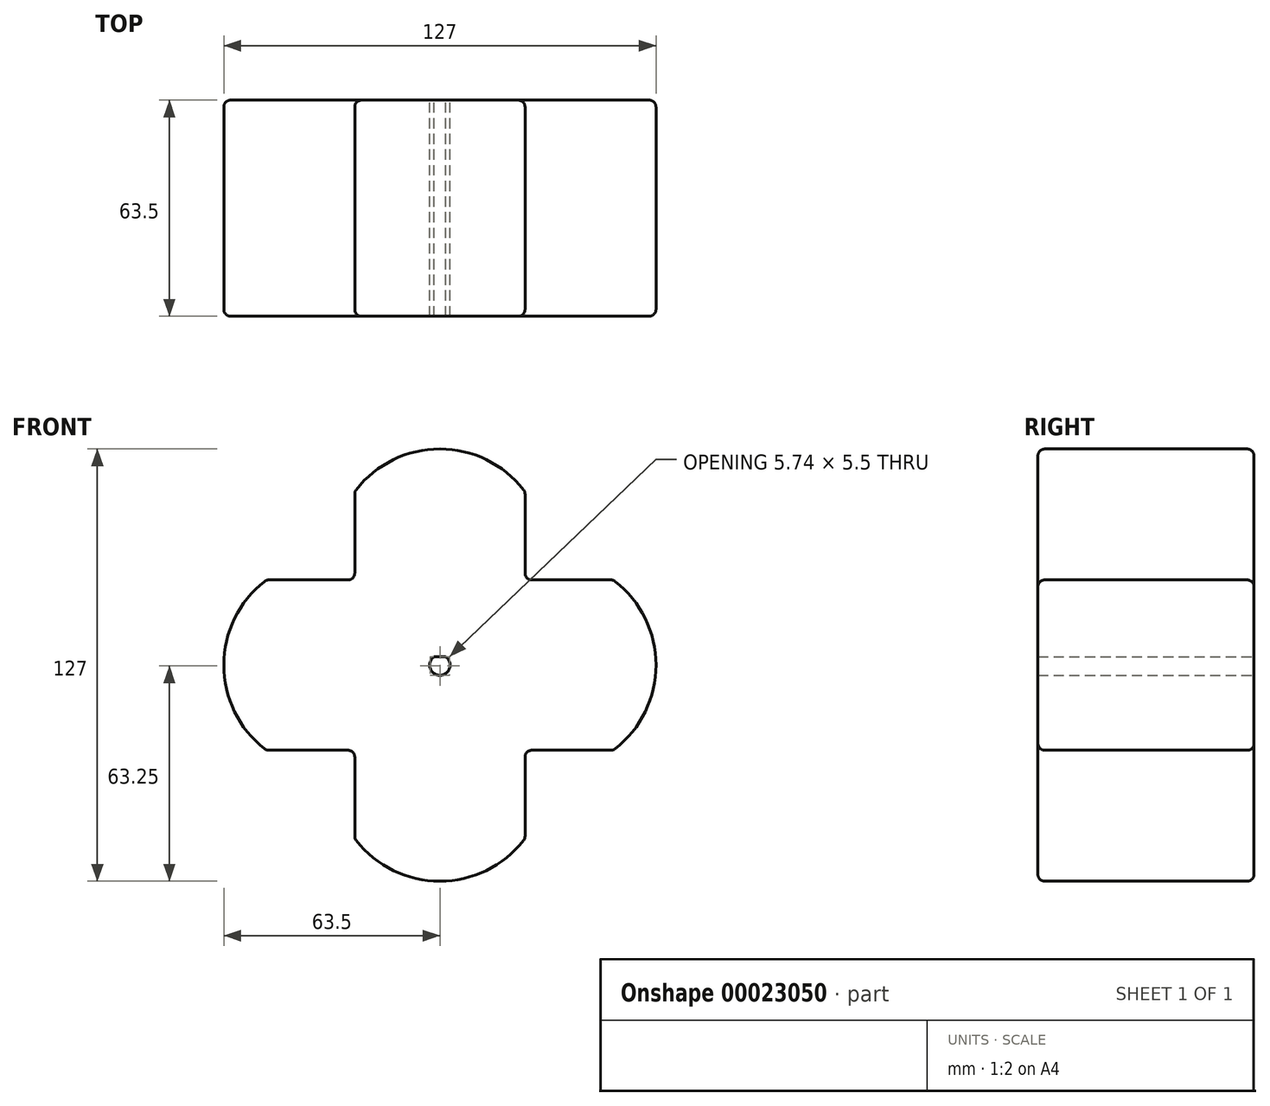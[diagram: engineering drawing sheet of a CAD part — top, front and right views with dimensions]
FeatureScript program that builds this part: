
annotation { "Feature Type Name" : "Feature", "Feature Type Description" : "" }
export const myFeature = defineFeature(function(context is Context, id is Id, definition is map)
    precondition{}
    {
        {
            var Q0;
            Q0=qCreatedBy(makeId("Front.planeOp"),FACE);
            var sketch = newSketch(context, id + "F0", { "sketchPlane" : qUnion([Q0])});
            skLineSegment(sketch, "E0", {"start": v(0, 63.5) * mm, "end": v(0, 0) * mm});
            skLineSegment(sketch, "E1", {"start": v(0, 0) * mm, "end": v(0, -63.5) * mm});
            skPoint(sketch, "E2", {"position": v(-38.48, 0) * mm});
            skPoint(sketch, "E3", {"position": v(0, 38.48) * mm});
            skPoint(sketch, "E4", {"position": v(38.48, 0) * mm});
            skPoint(sketch, "E5", {"position": v(0, -38.48) * mm});
            skLineSegment(sketch, "E6", {"start": v(-38.48, 25.02) * mm, "end": v(-25.02, 25.02) * mm});
            skLineSegment(sketch, "E7", {"start": v(-38.48, -25.02) * mm, "end": v(-25.02, -25.02) * mm});
            skLineSegment(sketch, "E8", {"start": v(-25.02, 38.48) * mm, "end": v(-25.02, 25.02) * mm});
            skLineSegment(sketch, "E9", {"start": v(25.02, 38.48) * mm, "end": v(25.02, 25.02) * mm});
            skLineSegment(sketch, "E10.trimOffspring", {"start": v(25.02, 25.02) * mm, "end": v(38.48, 25.02) * mm});
            skLineSegment(sketch, "E11.trimOffspring", {"start": v(25.02, 0) * mm, "end": v(63.5, 0) * mm});
            skLineSegment(sketch, "E12.trimOffspring", {"start": v(-25.02, 0) * mm, "end": v(-63.5, 0) * mm});
            skLineSegment(sketch, "E13.trimOffspring", {"start": v(25.02, -25.02) * mm, "end": v(38.48, -25.02) * mm});
            skLineSegment(sketch, "E14.trimOffspring", {"start": v(-25.02, -25.02) * mm, "end": v(-25.02, -38.48) * mm});
            skLineSegment(sketch, "E15.trimOffspring", {"start": v(25.02, -25.02) * mm, "end": v(25.02, -38.48) * mm});
            skPoint(sketch, "E16", {"position": v(0, -51) * mm});
            skPoint(sketch, "E17", {"position": v(-51, 0) * mm});
            skPoint(sketch, "E18", {"position": v(51, 0) * mm});
            skPoint(sketch, "E19", {"position": v(0, 51) * mm});
            skLineSegment(sketch, "E20", {"start": v(-38.48, 25.02) * mm, "end": v(-51, 25.02) * mm});
            skLineSegment(sketch, "E21", {"start": v(-38.48, -25.02) * mm, "end": v(-51, -25.02) * mm});
            skLineSegment(sketch, "E22", {"start": v(-25.02, -38.48) * mm, "end": v(-25.02, -51) * mm});
            skLineSegment(sketch, "E23", {"start": v(25.02, -38.48) * mm, "end": v(25.02, -51) * mm});
            skLineSegment(sketch, "E24", {"start": v(38.48, -25.02) * mm, "end": v(51, -25.02) * mm});
            skLineSegment(sketch, "E25", {"start": v(38.48, 25.02) * mm, "end": v(51, 25.02) * mm});
            skLineSegment(sketch, "E26", {"start": v(25.02, 38.48) * mm, "end": v(25.02, 51) * mm});
            skLineSegment(sketch, "E27", {"start": v(-25.02, 38.48) * mm, "end": v(-25.02, 51) * mm});
            skArc(sketch, "E28", {"start": v(-51, 25.02) * mm, "mid": v(-63.5, 0) * mm, "end": v(-51, -25.02) * mm});
            skArc(sketch, "E29", {"start": v(25.02, 51) * mm, "mid": v(0, 63.5) * mm, "end": v(-25.02, 51) * mm});
            skArc(sketch, "E30", {"start": v(51, -25.02) * mm, "mid": v(63.5, 0) * mm, "end": v(51, 25.02) * mm});
            skArc(sketch, "E31", {"start": v(-25.02, -51) * mm, "mid": v(0, -63.5) * mm, "end": v(25.02, -51) * mm});
            skArc(sketch, "E32", {"start": v(-1.66, 2.5) * mm, "mid": v(0, -3) * mm, "end": v(1.66, 2.5) * mm});
            skLineSegment(sketch, "E33", {"start": v(0, 2.5) * mm, "end": v(1.66, 2.5) * mm});
            skLineSegment(sketch, "E34", {"start": v(1.66, 2.5) * mm, "end": v(-1.66, 2.5) * mm});
            skSolve(sketch);
        }
        {
            var Q0;
            Q0 = qSketchRegion(id + "F0", true);
            extrude(context, id + "F1", {"entities" : qUnion([Q0]), "depth" : 63.5 * mm});
        }
        {
            var Q0;
            Q0=makeQuery(id+"F1.opExtrude","CAP_EDGE",EDGE,{"disambiguationData":[OSD([sQuery(id+"F0.wireOp",EDGE,"E8"),sQuery(id+"F0.wireOp",EDGE,"E27")])],"isStart":false});
            var Q1;
            Q1=makeQuery(id+"F1.opExtrude","CAP_EDGE",EDGE,{"disambiguationData":[OSD([sQuery(id+"F0.wireOp",EDGE,"E6"),sQuery(id+"F0.wireOp",EDGE,"E20")])],"isStart":false});
            var Q2;
            Q2=makeQuery(id+"F1.opExtrude","CAP_EDGE",EDGE,{"disambiguationData":[OSD([sQuery(id+"F0.wireOp",EDGE,"E29")])],"isStart":false});
            var Q3;
            Q3=makeQuery(id+"F1.opExtrude","CAP_EDGE",EDGE,{"disambiguationData":[OSD([sQuery(id+"F0.wireOp",EDGE,"E10.trimOffspring"),sQuery(id+"F0.wireOp",EDGE,"E25")])],"isStart":false});
            var Q4;
            Q4=makeQuery(id+"F1.opExtrude","CAP_EDGE",EDGE,{"disambiguationData":[OSD([sQuery(id+"F0.wireOp",EDGE,"E9"),sQuery(id+"F0.wireOp",EDGE,"E26")])],"isStart":false});
            var Q5;
            Q5=makeQuery(id+"F1.opExtrude","CAP_EDGE",EDGE,{"disambiguationData":[OSD([sQuery(id+"F0.wireOp",EDGE,"E29")])],"isStart":true});
            var Q6;
            Q6=makeQuery(id+"F1.opExtrude","CAP_EDGE",EDGE,{"disambiguationData":[OSD([sQuery(id+"F0.wireOp",EDGE,"E9"),sQuery(id+"F0.wireOp",EDGE,"E26")])],"isStart":true});
            var Q7;
            Q7=makeQuery(id+"F1.opExtrude","CAP_EDGE",EDGE,{"disambiguationData":[OSD([sQuery(id+"F0.wireOp",EDGE,"E6"),sQuery(id+"F0.wireOp",EDGE,"E20")])],"isStart":true});
            var Q8;
            Q8=makeQuery(id+"F1.opExtrude","CAP_EDGE",EDGE,{"disambiguationData":[OSD([sQuery(id+"F0.wireOp",EDGE,"E8"),sQuery(id+"F0.wireOp",EDGE,"E27")])],"isStart":true});
            var Q9;
            Q9=makeQuery(id+"F1.opExtrude","CAP_EDGE",EDGE,{"disambiguationData":[OSD([sQuery(id+"F0.wireOp",EDGE,"E10.trimOffspring"),sQuery(id+"F0.wireOp",EDGE,"E25")])],"isStart":true});
            var Q10;
            Q10=makeQuery(id+"F1.opExtrude","CAP_EDGE",EDGE,{"disambiguationData":[OSD([sQuery(id+"F0.wireOp",EDGE,"E15.trimOffspring"),sQuery(id+"F0.wireOp",EDGE,"E23")])],"isStart":false});
            var Q11;
            Q11=makeQuery(id+"F1.opExtrude","CAP_EDGE",EDGE,{"disambiguationData":[OSD([sQuery(id+"F0.wireOp",EDGE,"E14.trimOffspring"),sQuery(id+"F0.wireOp",EDGE,"E22")])],"isStart":false});
            var Q12;
            Q12=makeQuery(id+"F1.opExtrude","CAP_EDGE",EDGE,{"disambiguationData":[OSD([sQuery(id+"F0.wireOp",EDGE,"E13.trimOffspring"),sQuery(id+"F0.wireOp",EDGE,"E24")])],"isStart":false});
            var Q13;
            Q13=makeQuery(id+"F1.opExtrude","CAP_EDGE",EDGE,{"disambiguationData":[OSD([sQuery(id+"F0.wireOp",EDGE,"E7"),sQuery(id+"F0.wireOp",EDGE,"E21")])],"isStart":false});
            var Q14;
            Q14=makeQuery(id+"F1.opExtrude","CAP_EDGE",EDGE,{"disambiguationData":[OSD([sQuery(id+"F0.wireOp",EDGE,"E31")])],"isStart":false});
            var Q15;
            Q15=makeQuery(id+"F1.opExtrude","CAP_EDGE",EDGE,{"disambiguationData":[OSD([sQuery(id+"F0.wireOp",EDGE,"E31")])],"isStart":true});
            var Q16;
            Q16=makeQuery(id+"F1.opExtrude","CAP_EDGE",EDGE,{"disambiguationData":[OSD([sQuery(id+"F0.wireOp",EDGE,"E7"),sQuery(id+"F0.wireOp",EDGE,"E21")])],"isStart":true});
            var Q17;
            Q17=makeQuery(id+"F1.opExtrude","CAP_EDGE",EDGE,{"disambiguationData":[OSD([sQuery(id+"F0.wireOp",EDGE,"E15.trimOffspring"),sQuery(id+"F0.wireOp",EDGE,"E23")])],"isStart":true});
            var Q18;
            Q18=makeQuery(id+"F1.opExtrude","CAP_EDGE",EDGE,{"disambiguationData":[OSD([sQuery(id+"F0.wireOp",EDGE,"E14.trimOffspring"),sQuery(id+"F0.wireOp",EDGE,"E22")])],"isStart":true});
            var Q19;
            Q19=makeQuery(id+"F1.opExtrude","CAP_EDGE",EDGE,{"disambiguationData":[OSD([sQuery(id+"F0.wireOp",EDGE,"E13.trimOffspring"),sQuery(id+"F0.wireOp",EDGE,"E24")])],"isStart":true});
            var Q20;
            Q20=makeQuery(id+"F1.opExtrude","CAP_EDGE",EDGE,{"disambiguationData":[OSD([sQuery(id+"F0.wireOp",EDGE,"E30")])],"isStart":false});
            var Q21;
            Q21=makeQuery(id+"F1.opExtrude","CAP_EDGE",EDGE,{"disambiguationData":[OSD([sQuery(id+"F0.wireOp",EDGE,"E30")])],"isStart":true});
            var Q22;
            Q22=makeQuery(id+"F1.opExtrude","CAP_EDGE",EDGE,{"disambiguationData":[OSD([sQuery(id+"F0.wireOp",EDGE,"E28")])],"isStart":false});
            var Q23;
            Q23=makeQuery(id+"F1.opExtrude","CAP_EDGE",EDGE,{"disambiguationData":[OSD([sQuery(id+"F0.wireOp",EDGE,"E28")])],"isStart":true});
            var Q24;
            Q24=makeQuery(id+"F1.opExtrude","SWEPT_EDGE",EDGE,{"disambiguationData":[OSD([sQuery(id+"F0.wireOp",EDGE,"E20"),sQuery(id+"F0.wireOp",EDGE,"E28")])]});
            var Q25;
            Q25=makeQuery(id+"F1.opExtrude","SWEPT_EDGE",EDGE,{"disambiguationData":[OSD([sQuery(id+"F0.wireOp",EDGE,"E27"),sQuery(id+"F0.wireOp",EDGE,"E29")])]});
            var Q26;
            Q26=makeQuery(id+"F1.opExtrude","SWEPT_EDGE",EDGE,{"disambiguationData":[OSD([sQuery(id+"F0.wireOp",EDGE,"E26"),sQuery(id+"F0.wireOp",EDGE,"E29")])]});
            var Q27;
            Q27=makeQuery(id+"F1.opExtrude","SWEPT_EDGE",EDGE,{"disambiguationData":[OSD([sQuery(id+"F0.wireOp",EDGE,"E6"),sQuery(id+"F0.wireOp",EDGE,"E8")])]});
            var Q28;
            Q28=makeQuery(id+"F1.opExtrude","SWEPT_EDGE",EDGE,{"disambiguationData":[OSD([sQuery(id+"F0.wireOp",EDGE,"E9"),sQuery(id+"F0.wireOp",EDGE,"E10.trimOffspring")])]});
            var Q29;
            Q29=makeQuery(id+"F1.opExtrude","SWEPT_EDGE",EDGE,{"disambiguationData":[OSD([sQuery(id+"F0.wireOp",EDGE,"E25"),sQuery(id+"F0.wireOp",EDGE,"E30")])]});
            var Q30;
            Q30=makeQuery(id+"F1.opExtrude","SWEPT_EDGE",EDGE,{"disambiguationData":[OSD([sQuery(id+"F0.wireOp",EDGE,"E22"),sQuery(id+"F0.wireOp",EDGE,"E31")])]});
            var Q31;
            Q31=makeQuery(id+"F1.opExtrude","SWEPT_EDGE",EDGE,{"disambiguationData":[OSD([sQuery(id+"F0.wireOp",EDGE,"E21"),sQuery(id+"F0.wireOp",EDGE,"E28")])]});
            var Q32;
            Q32=makeQuery(id+"F1.opExtrude","SWEPT_EDGE",EDGE,{"disambiguationData":[OSD([sQuery(id+"F0.wireOp",EDGE,"E23"),sQuery(id+"F0.wireOp",EDGE,"E31")])]});
            var Q33;
            Q33=makeQuery(id+"F1.opExtrude","SWEPT_EDGE",EDGE,{"disambiguationData":[OSD([sQuery(id+"F0.wireOp",EDGE,"E7"),sQuery(id+"F0.wireOp",EDGE,"E14.trimOffspring")])]});
            var Q34;
            Q34=makeQuery(id+"F1.opExtrude","SWEPT_EDGE",EDGE,{"disambiguationData":[OSD([sQuery(id+"F0.wireOp",EDGE,"E13.trimOffspring"),sQuery(id+"F0.wireOp",EDGE,"E15.trimOffspring")])]});
            var Q35;
            Q35=makeQuery(id+"F1.opExtrude","SWEPT_EDGE",EDGE,{"disambiguationData":[OSD([sQuery(id+"F0.wireOp",EDGE,"E24"),sQuery(id+"F0.wireOp",EDGE,"E30")])]});
            fillet(context, id + "F2", {"entities" : qUnion([Q0, Q1, Q2, Q3, Q4, Q5, Q6, Q7, Q8, Q9, Q10, Q11, Q12, Q13, Q14, Q15, Q16, Q17, Q18, Q19, Q20, Q21, Q22, Q23, Q24, Q25, Q26, Q27, Q28, Q29, Q30, Q31, Q32, Q33, Q34, Q35]), "radius" : 2 * mm, "tangentPropagation" : true, "allowEdgeOverflow" : false});
        }
    });
